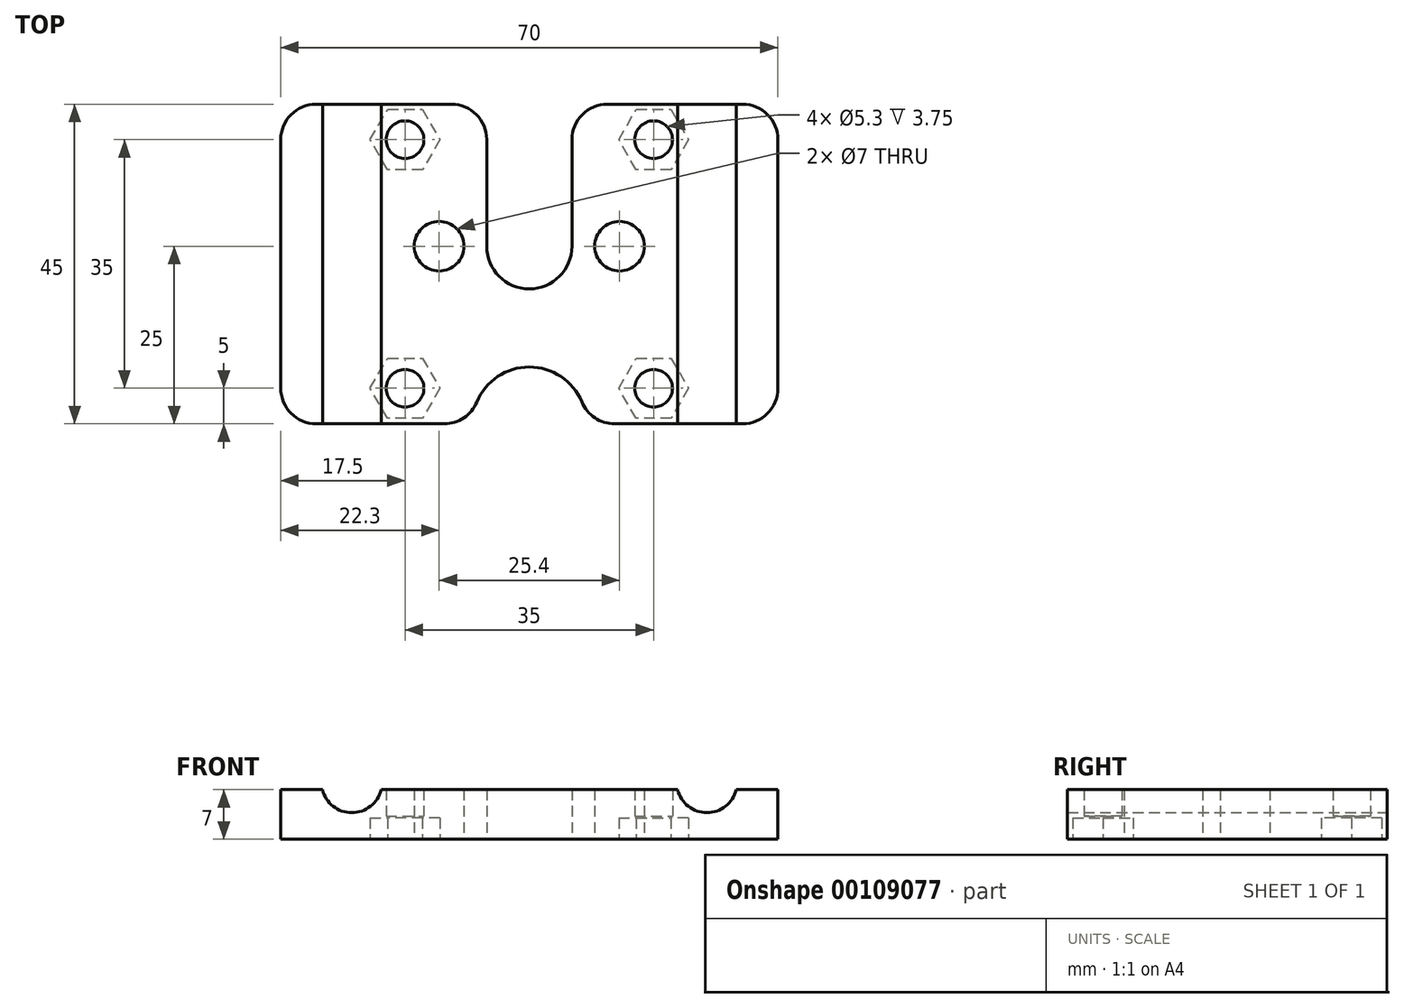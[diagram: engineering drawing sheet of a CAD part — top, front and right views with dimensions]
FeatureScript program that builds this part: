
annotation { "Feature Type Name" : "Feature", "Feature Type Description" : "" }
export const myFeature = defineFeature(function(context is Context, id is Id, definition is map)
    precondition{}
    {
        {
            var Q0;
            Q0=qCreatedBy(makeId("Top.planeOp"),FACE);
            var sketch = newSketch(context, id + "F0", { "sketchPlane" : qUnion([Q0])});
            skLineSegment(sketch, "E0.bottom", {"start": v(-35, 22.5) * mm, "end": v(-6, 22.5) * mm});
            skLineSegment(sketch, "E0.top", {"start": v(-35, -22.5) * mm, "end": v(-8, -22.5) * mm});
            skLineSegment(sketch, "E0.left", {"start": v(-35, 22.5) * mm, "end": v(-35, -22.5) * mm});
            skLineSegment(sketch, "E0.right", {"start": v(35, 22.5) * mm, "end": v(35, -22.5) * mm});
            skPoint(sketch, "E0.middle", {"position": v(0, 0) * mm});
            skLineSegment(sketch, "E1", {"start": v(-6, 22.5) * mm, "end": v(-6, 2.5) * mm});
            skLineSegment(sketch, "E2", {"start": v(6, 22.5) * mm, "end": v(6, 2.5) * mm});
            skLineSegment(sketch, "E3", {"start": v(0, 32.8) * mm, "end": v(0, -32.8) * mm, "construction": true});
            skLineSegment(sketch, "E4.bottom", {"start": v(17.5, -17.5) * mm, "end": v(-17.5, -17.5) * mm, "construction": true});
            skLineSegment(sketch, "E4.top", {"start": v(17.5, 17.5) * mm, "end": v(-17.5, 17.5) * mm, "construction": true});
            skLineSegment(sketch, "E4.left", {"start": v(17.5, -17.5) * mm, "end": v(17.5, 17.5) * mm, "construction": true});
            skLineSegment(sketch, "E4.right", {"start": v(-17.5, -17.5) * mm, "end": v(-17.5, 17.5) * mm, "construction": true});
            skArc(sketch, "E5", {"start": v(-6, 2.5) * mm, "mid": v(0, -3.5) * mm, "end": v(6, 2.5) * mm});
            skLineSegment(sketch, "E6.trimOffspring", {"start": v(6, 22.5) * mm, "end": v(35, 22.5) * mm});
            skCircle(sketch, "E7", {"center": v(-17.5, 17.5) * mm, "radius": 2.65 * mm});
            skCircle(sketch, "E8", {"center": v(-17.5, -17.5) * mm, "radius": 2.65 * mm});
            skCircle(sketch, "E9", {"center": v(17.5, 17.5) * mm, "radius": 2.65 * mm});
            skCircle(sketch, "E10", {"center": v(17.5, -17.5) * mm, "radius": 2.65 * mm});
            skArc(sketch, "E11", {"start": v(8, -22.5) * mm, "mid": v(0, -14.5) * mm, "end": v(-8, -22.5) * mm});
            skLineSegment(sketch, "E12.trimOffspring", {"start": v(8, -22.5) * mm, "end": v(35, -22.5) * mm});
            skCircle(sketch, "E13.cCircle", {"center": v(-17.5, 17.5) * mm, "radius": 4.25 * mm, "construction": true});
            skLineSegment(sketch, "E13.0", {"start": v(-15.05, 13.25) * mm, "end": v(-19.95, 13.25) * mm});
            skLineSegment(sketch, "E13.1", {"start": v(-19.95, 13.25) * mm, "end": v(-22.4, 17.5) * mm});
            skLineSegment(sketch, "E13.2", {"start": v(-22.4, 17.5) * mm, "end": v(-19.95, 21.75) * mm});
            skLineSegment(sketch, "E13.3", {"start": v(-19.95, 21.75) * mm, "end": v(-15.05, 21.75) * mm});
            skLineSegment(sketch, "E13.4", {"start": v(-15.05, 21.75) * mm, "end": v(-12.6, 17.5) * mm});
            skLineSegment(sketch, "E13.5", {"start": v(-12.6, 17.5) * mm, "end": v(-15.05, 13.25) * mm});
            skPoint(sketch, "E13.0.midPoint", {"position": v(-17.5, 13.25) * mm});
            skCircle(sketch, "E14.cCircle", {"center": v(-17.5, -17.5) * mm, "radius": 4.25 * mm, "construction": true});
            skLineSegment(sketch, "E14.0", {"start": v(-19.95, -13.25) * mm, "end": v(-15.05, -13.25) * mm});
            skLineSegment(sketch, "E14.1", {"start": v(-15.05, -13.25) * mm, "end": v(-12.6, -17.5) * mm});
            skLineSegment(sketch, "E14.2", {"start": v(-12.6, -17.5) * mm, "end": v(-15.05, -21.75) * mm});
            skLineSegment(sketch, "E14.3", {"start": v(-15.05, -21.75) * mm, "end": v(-19.95, -21.75) * mm});
            skLineSegment(sketch, "E14.4", {"start": v(-19.95, -21.75) * mm, "end": v(-22.4, -17.5) * mm});
            skLineSegment(sketch, "E14.5", {"start": v(-22.4, -17.5) * mm, "end": v(-19.95, -13.25) * mm});
            skPoint(sketch, "E14.0.midPoint", {"position": v(-17.5, -13.25) * mm});
            skCircle(sketch, "E15.cCircle", {"center": v(17.5, -17.5) * mm, "radius": 4.25 * mm, "construction": true});
            skLineSegment(sketch, "E15.0", {"start": v(15.05, -13.25) * mm, "end": v(19.95, -13.25) * mm});
            skLineSegment(sketch, "E15.1", {"start": v(19.95, -13.25) * mm, "end": v(22.4, -17.5) * mm});
            skLineSegment(sketch, "E15.2", {"start": v(22.4, -17.5) * mm, "end": v(19.95, -21.75) * mm});
            skLineSegment(sketch, "E15.3", {"start": v(19.95, -21.75) * mm, "end": v(15.05, -21.75) * mm});
            skLineSegment(sketch, "E15.4", {"start": v(15.05, -21.75) * mm, "end": v(12.6, -17.5) * mm});
            skLineSegment(sketch, "E15.5", {"start": v(12.6, -17.5) * mm, "end": v(15.05, -13.25) * mm});
            skPoint(sketch, "E15.0.midPoint", {"position": v(17.5, -13.25) * mm});
            skCircle(sketch, "E16.cCircle", {"center": v(17.5, 17.5) * mm, "radius": 4.25 * mm, "construction": true});
            skLineSegment(sketch, "E16.0", {"start": v(19.95, 13.25) * mm, "end": v(15.05, 13.25) * mm});
            skLineSegment(sketch, "E16.1", {"start": v(15.05, 13.25) * mm, "end": v(12.6, 17.5) * mm});
            skLineSegment(sketch, "E16.2", {"start": v(12.6, 17.5) * mm, "end": v(15.05, 21.75) * mm});
            skLineSegment(sketch, "E16.3", {"start": v(15.05, 21.75) * mm, "end": v(19.95, 21.75) * mm});
            skLineSegment(sketch, "E16.4", {"start": v(19.95, 21.75) * mm, "end": v(22.4, 17.5) * mm});
            skLineSegment(sketch, "E16.5", {"start": v(22.4, 17.5) * mm, "end": v(19.95, 13.25) * mm});
            skPoint(sketch, "E16.0.midPoint", {"position": v(17.5, 13.25) * mm});
            skLineSegment(sketch, "E17", {"start": v(46.48, 0) * mm, "end": v(-46.48, 0) * mm, "construction": true});
            skPoint(sketch, "E18", {"position": v(35, 0) * mm});
            skPoint(sketch, "E19", {"position": v(-35, 0) * mm});
            skLineSegment(sketch, "E20", {"start": v(17.5, 17.5) * mm, "end": v(-17.5, -17.5) * mm, "construction": true});
            skLineSegment(sketch, "E21", {"start": v(12.7, 2.5) * mm, "end": v(-12.7, 2.5) * mm, "construction": true});
            skCircle(sketch, "E22", {"center": v(12.7, 2.5) * mm, "radius": 3.5 * mm});
            skCircle(sketch, "E23", {"center": v(-12.7, 2.5) * mm, "radius": 3.5 * mm});
            skSolve(sketch);
        }
        {
            var Q0;
            Q0=makeQuery(id+"F0.imprint","IMPRINT",FACE,{"disambiguationData":[TD([[makeQuery(id+"F0.imprint","IMPRINT",EDGE,{"derivedFrom":sQuery(id+"F0.wireOp",EDGE,"E0.bottom")}),-1.0]])]});
            var Q1;
            Q1=makeQuery(id+"F0.imprint","IMPRINT",FACE,{"disambiguationData":[TD([[makeQuery(id+"F0.imprint","IMPRINT",EDGE,{"derivedFrom":sQuery(id+"F0.wireOp",EDGE,"E7")}),-1.0]])]});
            var Q2;
            Q2=makeQuery(id+"F0.imprint","IMPRINT",FACE,{"disambiguationData":[TD([[makeQuery(id+"F0.imprint","IMPRINT",EDGE,{"derivedFrom":sQuery(id+"F0.wireOp",EDGE,"E8")}),-1.0]])]});
            var Q3;
            Q3=makeQuery(id+"F0.imprint","IMPRINT",FACE,{"disambiguationData":[TD([[makeQuery(id+"F0.imprint","IMPRINT",EDGE,{"derivedFrom":sQuery(id+"F0.wireOp",EDGE,"E10")}),-1.0]])]});
            var Q4;
            Q4=makeQuery(id+"F0.imprint","IMPRINT",FACE,{"disambiguationData":[TD([[makeQuery(id+"F0.imprint","IMPRINT",EDGE,{"derivedFrom":sQuery(id+"F0.wireOp",EDGE,"E9")}),-1.0]])]});
            extrude(context, id + "F1", {"entities" : qUnion([Q0, Q1, Q2, Q3, Q4]), "depth" : 7 * mm});
        }
        {
            var Q0;
            Q0=makeQuery(id+"F0.imprint","IMPRINT",FACE,{"disambiguationData":[TD([[makeQuery(id+"F0.imprint","IMPRINT",EDGE,{"derivedFrom":sQuery(id+"F0.wireOp",EDGE,"E10")}),-1.0]])]});
            var Q1;
            Q1=makeQuery(id+"F0.imprint","IMPRINT",FACE,{"disambiguationData":[TD([[makeQuery(id+"F0.imprint","IMPRINT",EDGE,{"derivedFrom":sQuery(id+"F0.wireOp",EDGE,"E9")}),-1.0]])]});
            var Q2;
            Q2=makeQuery(id+"F0.imprint","IMPRINT",FACE,{"disambiguationData":[TD([[makeQuery(id+"F0.imprint","IMPRINT",EDGE,{"derivedFrom":sQuery(id+"F0.wireOp",EDGE,"E7")}),-1.0]])]});
            var Q3;
            Q3=makeQuery(id+"F0.imprint","IMPRINT",FACE,{"disambiguationData":[TD([[makeQuery(id+"F0.imprint","IMPRINT",EDGE,{"derivedFrom":sQuery(id+"F0.wireOp",EDGE,"E8")}),-1.0]])]});
            extrude(context, id + "F2", {"entities" : qUnion([Q0, Q1, Q2, Q3]), "operationType" : NewBodyOperationType.REMOVE, "depth" : 3 * mm});
        }
        {
            var Q0;
            Q0=makeQuery(id+"F1.opExtrude","SWEPT_FACE",FACE,{"disambiguationData":[OSD([sQuery(id+"F0.wireOp",EDGE,"E6.trimOffspring")])]});
            var sketch = newSketch(context, id + "F3", { "sketchPlane" : qUnion([Q0])});
            skLineSegment(sketch, "E24", {"start": v(0, 23) * mm, "end": v(0, -12.51) * mm, "construction": true});
            skCircle(sketch, "E25", {"center": v(-25, 8) * mm, "radius": 4.25 * mm});
            skCircle(sketch, "E26.MirrorC", {"center": v(25, 8) * mm, "radius": 4.25 * mm});
            skSolve(sketch);
        }
        {
            var Q0;
            Q0 = qSketchRegion(id + "F3", true);
            extrude(context, id + "F4", {"entities" : qUnion([Q0]), "operationType" : NewBodyOperationType.REMOVE, "endBound" : BoundingType.THROUGH_ALL, "oppositeDirection" : true, "depth" : 25 * mm});
        }
        {
            var Q0;
            Q0=makeQuery(id+"F1.opExtrude","SWEPT_EDGE",EDGE,{"disambiguationData":[OSD([sQuery(id+"F0.wireOp",EDGE,"E0.right"),sQuery(id+"F0.wireOp",EDGE,"E6.trimOffspring")])]});
            var Q1;
            Q1=makeQuery(id+"F1.opExtrude","SWEPT_EDGE",EDGE,{"disambiguationData":[OSD([sQuery(id+"F0.wireOp",EDGE,"E2"),sQuery(id+"F0.wireOp",EDGE,"E6.trimOffspring")])]});
            var Q2;
            Q2=makeQuery(id+"F1.opExtrude","SWEPT_EDGE",EDGE,{"disambiguationData":[OSD([sQuery(id+"F0.wireOp",EDGE,"E0.bottom"),sQuery(id+"F0.wireOp",EDGE,"E1")])]});
            var Q3;
            Q3=makeQuery(id+"F1.opExtrude","SWEPT_EDGE",EDGE,{"disambiguationData":[OSD([sQuery(id+"F0.wireOp",EDGE,"E0.bottom"),sQuery(id+"F0.wireOp",EDGE,"E0.left")])]});
            var Q4;
            Q4=makeQuery(id+"F1.opExtrude","SWEPT_EDGE",EDGE,{"disambiguationData":[OSD([sQuery(id+"F0.wireOp",EDGE,"E0.top"),sQuery(id+"F0.wireOp",EDGE,"E0.left")])]});
            var Q5;
            Q5=makeQuery(id+"F1.opExtrude","SWEPT_EDGE",EDGE,{"disambiguationData":[OSD([sQuery(id+"F0.wireOp",EDGE,"E0.right"),sQuery(id+"F0.wireOp",EDGE,"E12.trimOffspring")])]});
            var Q6;
            Q6=makeQuery(id+"F1.opExtrude","SWEPT_EDGE",EDGE,{"disambiguationData":[OSD([sQuery(id+"F0.wireOp",EDGE,"E0.top"),sQuery(id+"F0.wireOp",EDGE,"YmjCNWTm-jkmj-Voq9-geqU-ISEUDPNsSSp0")])]});
            var Q7;
            Q7=makeQuery(id+"F1.opExtrude","SWEPT_EDGE",EDGE,{"disambiguationData":[OSD([sQuery(id+"F0.wireOp",EDGE,"FJDRp5UC-pCl1-Of8g-wuzf-mFEpIjmOxVOe"),sQuery(id+"F0.wireOp",EDGE,"E12.trimOffspring")])]});
            fillet(context, id + "F5", {"entities" : qUnion([Q0, Q1, Q2, Q3, Q4, Q5, Q6, Q7]), "radius" : 5 * mm, "tangentPropagation" : true, "allowEdgeOverflow" : false});
        }
        {
            var Q0;
            Q0=makeQuery(id+"F2.boolean.opBoolean","COPY",FACE,{"derivedFrom":makeQuery(id+"F2.opExtrude","CAP_FACE",FACE,{"disambiguationData":[OSD([sQuery(id+"F0.wireOp",EDGE,"E9"),sQuery(id+"F0.wireOp",EDGE,"E16.0"),sQuery(id+"F0.wireOp",EDGE,"E16.1"),sQuery(id+"F0.wireOp",EDGE,"E16.2"),sQuery(id+"F0.wireOp",EDGE,"E16.3"),sQuery(id+"F0.wireOp",EDGE,"E16.4"),sQuery(id+"F0.wireOp",EDGE,"E16.5")])],"isStart":false})});
            cPlane(context, id + "F6", {"entities" : qUnion([Q0]), "cplaneType" : CPlaneType.OFFSET, "offset" : 0 * mm, "width" : 150 * mm, "height" : 150 * mm});
        }
        {
            var Q0;
            Q0=qCreatedBy(id+"F6.planeOp",FACE);
            var sketch = newSketch(context, id + "F7", { "sketchPlane" : qUnion([Q0])});
            skCircle(sketch, "E27.0", {"center": v(17.5, -17.5) * mm, "radius": 2.65 * mm});
            skCircle(sketch, "E28.0", {"center": v(17.5, 17.5) * mm, "radius": 2.65 * mm});
            skCircle(sketch, "E29.0", {"center": v(-17.5, 17.5) * mm, "radius": 2.65 * mm});
            skCircle(sketch, "E30.0", {"center": v(-17.5, -17.5) * mm, "radius": 2.65 * mm});
            skSolve(sketch);
        }
        {
            var Q0;
            Q0 = qSketchRegion(id + "F7", true);
            extrude(context, id + "F8", {"entities" : qUnion([Q0]), "operationType" : NewBodyOperationType.ADD, "oppositeDirection" : true, "depth" : .25 * mm});
        }
    });
